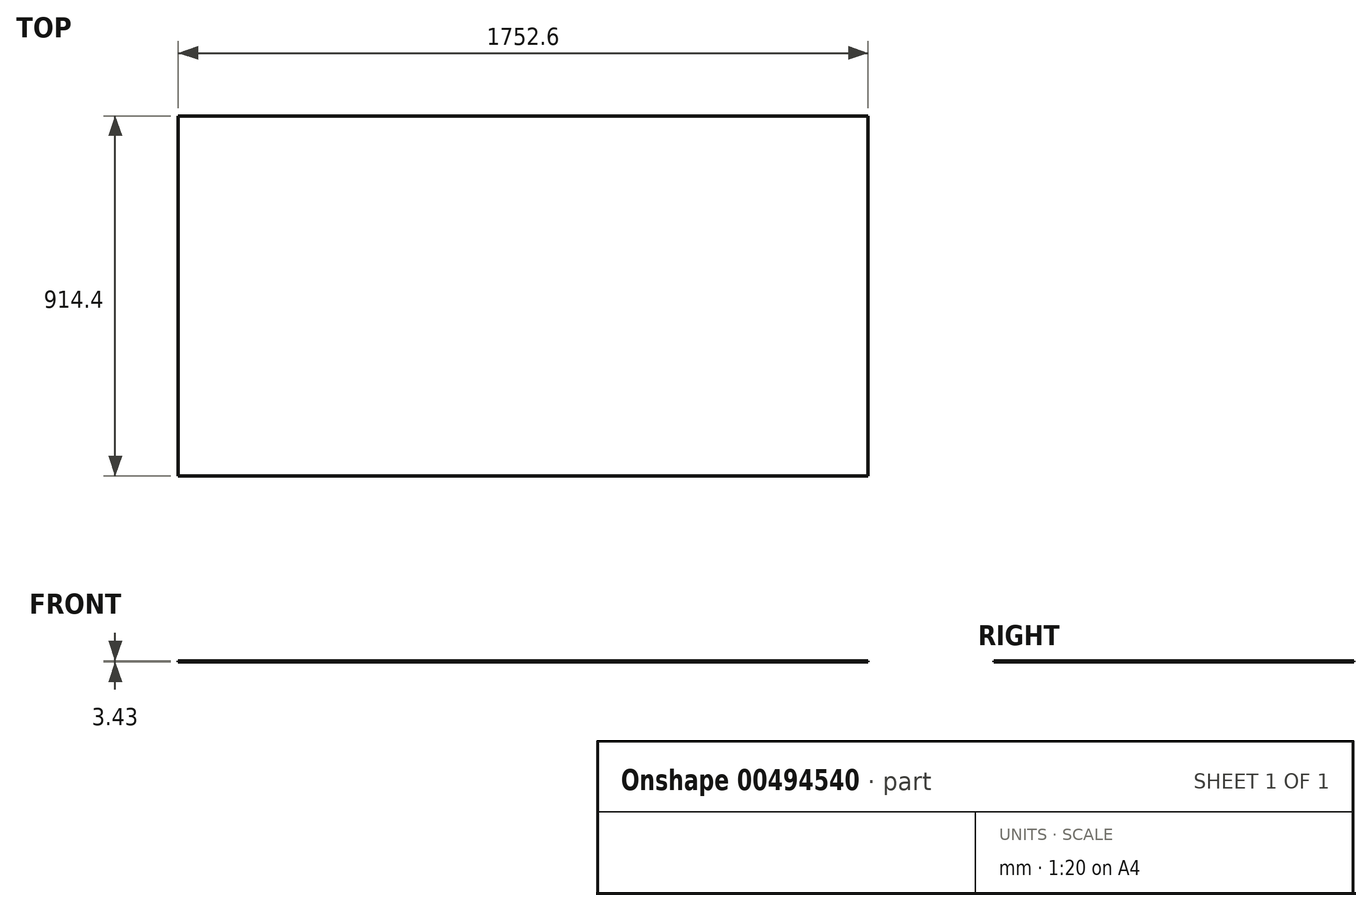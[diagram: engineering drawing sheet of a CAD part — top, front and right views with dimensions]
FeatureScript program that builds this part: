
annotation { "Feature Type Name" : "Feature", "Feature Type Description" : "" }
export const myFeature = defineFeature(function(context is Context, id is Id, definition is map)
    precondition{}
    {
        {
            var Q0;
            Q0=qCreatedBy(makeId("Top.planeOp"),FACE);
            var sketch = newSketch(context, id + "F0", { "sketchPlane" : qUnion([Q0])});
            skLineSegment(sketch, "E0.bottom", {"start": v(0, 0) * mm, "end": v(-1752.6, 0) * mm});
            skLineSegment(sketch, "E0.top", {"start": v(0, 914.4) * mm, "end": v(-1752.6, 914.4) * mm});
            skLineSegment(sketch, "E0.left", {"start": v(0, 0) * mm, "end": v(0, 914.4) * mm});
            skLineSegment(sketch, "E0.right", {"start": v(-1752.6, 0) * mm, "end": v(-1752.6, 914.4) * mm});
            skSolve(sketch);
        }
        {
            var Q0;
            Q0 = qSketchRegion(id + "F0", true);
            extrude(context, id + "F1", {"entities" : qUnion([Q0]), "depth" : 3.43 * mm});
        }
    });
